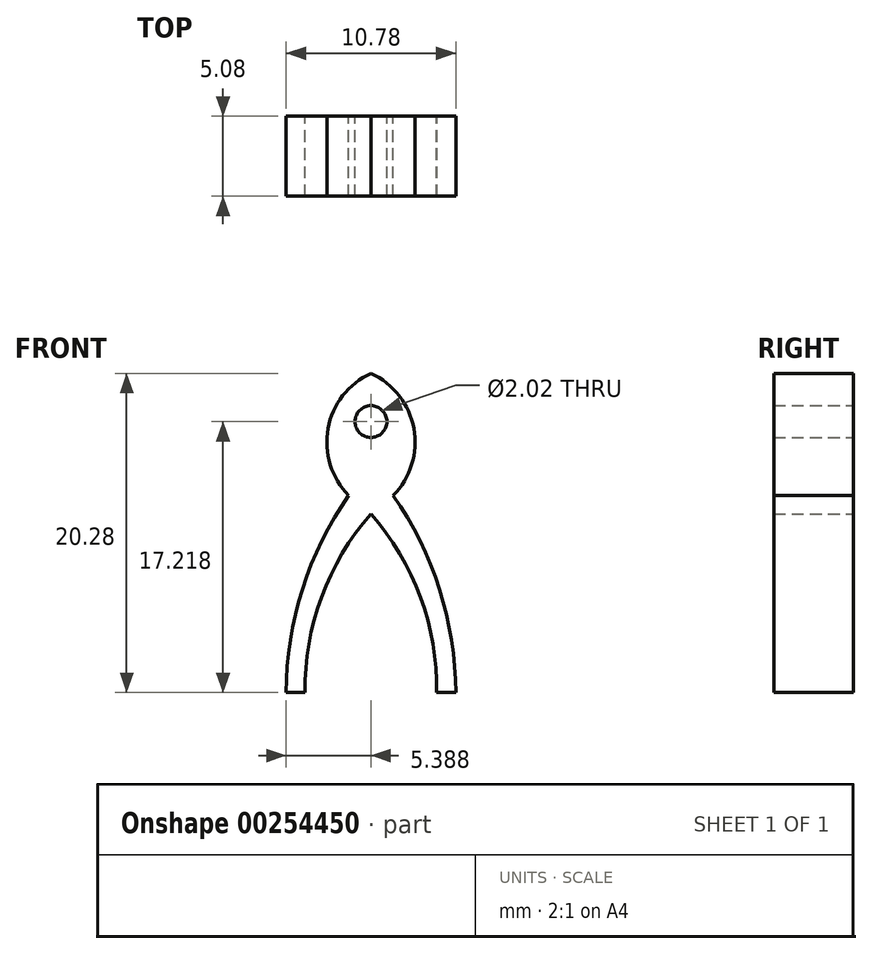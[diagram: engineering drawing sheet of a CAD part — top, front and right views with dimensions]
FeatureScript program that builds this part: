
annotation { "Feature Type Name" : "Feature", "Feature Type Description" : "" }
export const myFeature = defineFeature(function(context is Context, id is Id, definition is map)
    precondition{}
    {
        {
            var Q0;
            Q0=qCreatedBy(makeId("Front.planeOp"),FACE);
            var sketch = newSketch(context, id + "F0", { "sketchPlane" : qUnion([Q0])});
            skArc(sketch, "E0", {"start": v(5.39, 14.35) * mm, "mid": v(1.41, 7.66) * mm, "end": v(0, 0) * mm});
            skLineSegment(sketch, "E1", {"start": v(0, 0) * mm, "end": v(1.21, 0) * mm});
            skLineSegment(sketch, "E2", {"start": v(5.39, 14.35) * mm, "end": v(5.39, 11.35) * mm});
            skArc(sketch, "E3", {"start": v(5.39, 11.35) * mm, "mid": v(2.25, 6.06) * mm, "end": v(1.21, 0) * mm});
            skArc(sketch, "E4.MirrorCS", {"start": v(5.39, 14.35) * mm, "mid": v(9.37, 7.66) * mm, "end": v(10.78, 0) * mm});
            skArc(sketch, "E5.MirrorCS", {"start": v(5.39, 11.35) * mm, "mid": v(8.53, 6.06) * mm, "end": v(9.57, 0) * mm});
            skLineSegment(sketch, "E6.MirrorCS", {"start": v(10.78, 0) * mm, "end": v(9.57, 0) * mm});
            skArc(sketch, "E7", {"start": v(5.39, 20.28) * mm, "mid": v(2.66, 16.77) * mm, "end": v(3.97, 12.53) * mm});
            skLineSegment(sketch, "E8", {"start": v(5.39, 20.28) * mm, "end": v(5.39, 18.23) * mm});
            skLineSegment(sketch, "E9", {"start": v(5.39, 14.35) * mm, "end": v(5.39, 16.2) * mm});
            skArc(sketch, "E10", {"start": v(5.39, 18.23) * mm, "mid": v(4.38, 17.22) * mm, "end": v(5.39, 16.2) * mm});
            skArc(sketch, "E11.MirrorCS", {"start": v(5.39, 18.23) * mm, "mid": v(6.4, 17.22) * mm, "end": v(5.39, 16.2) * mm});
            skArc(sketch, "E12.MirrorCS", {"start": v(5.39, 20.28) * mm, "mid": v(8.11, 16.77) * mm, "end": v(6.8, 12.53) * mm});
            skSolve(sketch);
        }
        {
            var Q0;
            Q0 = qSketchRegion(id + "F0", true);
            extrude(context, id + "F1", {"entities" : qUnion([Q0]), "depth" : 5.08 * mm});
        }
    });
